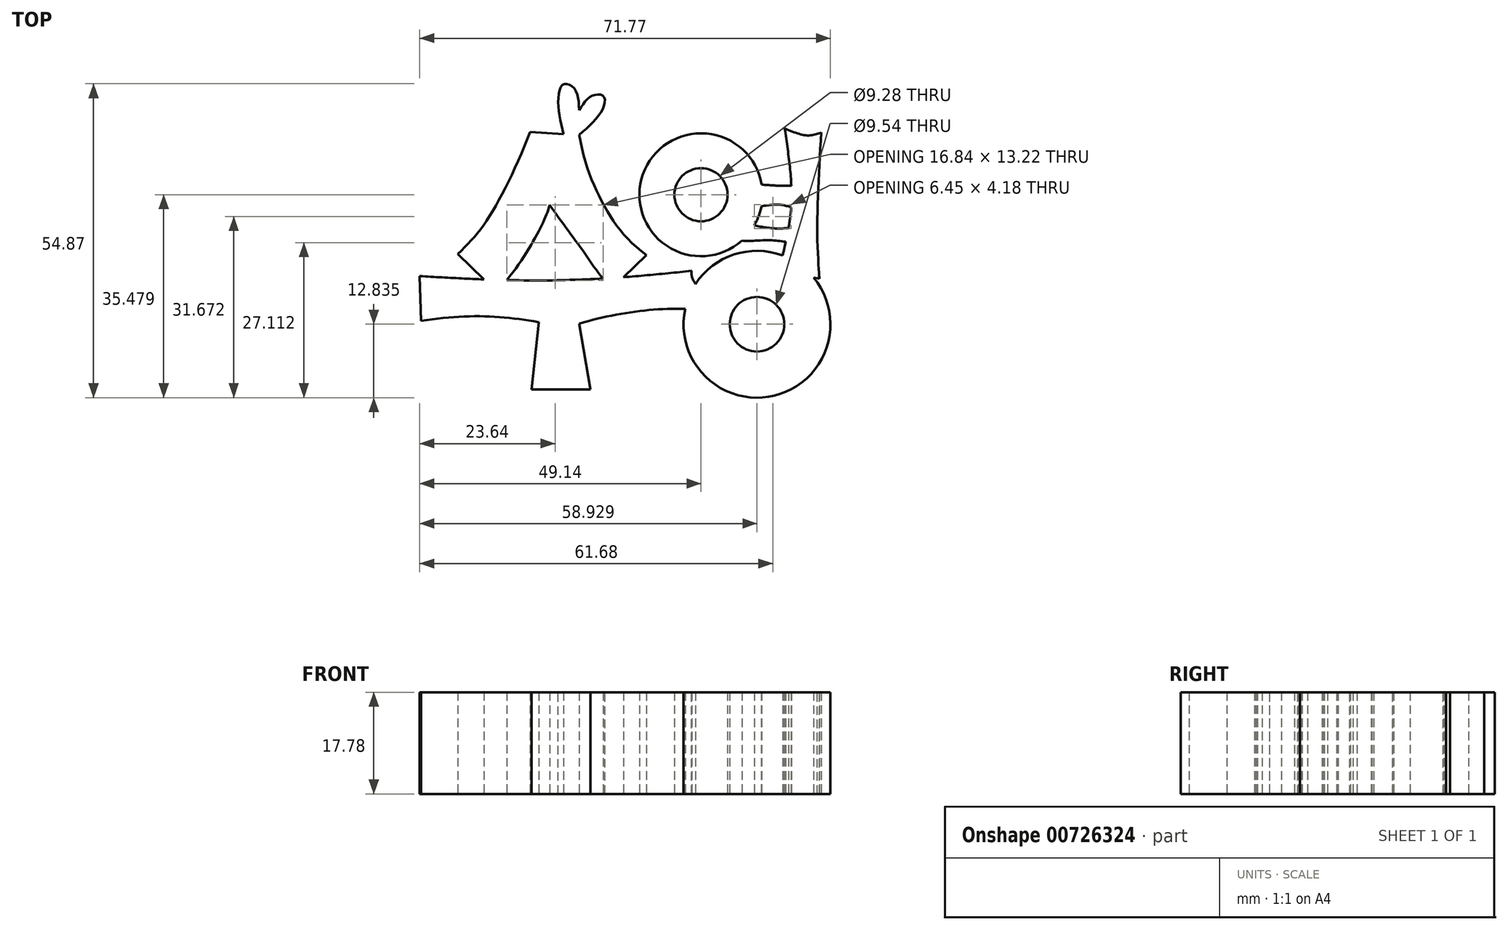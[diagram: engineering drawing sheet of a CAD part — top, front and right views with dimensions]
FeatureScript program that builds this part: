
annotation { "Feature Type Name" : "Feature", "Feature Type Description" : "" }
export const myFeature = defineFeature(function(context is Context, id is Id, definition is map)
    precondition{}
    {
        {
            var Q0;
            Q0=qCreatedBy(makeId("Top.planeOp"),FACE);
            var sketch = newSketch(context, id + "F0", { "sketchPlane" : qUnion([Q0])});
            skLineSegment(sketch, "E0", {"start": v(-29.82, 17.85) * mm, "end": v(-21.27, 17.36) * mm});
            skLineSegment(sketch, "E1", {"start": v(-42.52, -3.49) * mm, "end": v(-35.7, -10.02) * mm});
            skFitSpline(sketch, "E2", {"points": [v(-21.27, 17.36) * mm, v(-16.87, 4.89) * mm, v(-9.53, -3.67) * mm], "startDerivative": vector(4.76, -28.3) * mm, "endDerivative": vector(21.32, -15.57) * mm});
            skLineSegment(sketch, "E3", {"start": v(-9.53, -3.67) * mm, "end": v(-15.4, -9.29) * mm});
            skFitSpline(sketch, "E4", {"points": [v(-35.7, -10.02) * mm, v(-28.36, 0.49) * mm, v(-26.4, 5.13) * mm], "startDerivative": vector(15.3, 15.86) * mm, "endDerivative": vector(3.4, 11.19) * mm});
            skFitSpline(sketch, "E5", {"points": [v(-26.4, 5.13) * mm, v(-20.78, -2.69) * mm, v(-15.4, -9.29) * mm], "startDerivative": vector(10.2, -16.03) * mm, "endDerivative": vector(13.32, -9.78) * mm});
            skFitSpline(sketch, "E6", {"points": [v(-49.14, -7.33) * mm, v(-25.42, -8.07) * mm, v(-1.62, -6.4) * mm], "startDerivative": vector(47.36, -2.81) * mm, "endDerivative": vector(46.51, 5.27) * mm});
            skFitSpline(sketch, "E7", {"points": [v(-1.62, -6.4) * mm, v(0, -10.6) * mm, v(-1.1, -13.16) * mm], "startDerivative": vector(-1.95, -9.74) * mm, "endDerivative": vector(1.76, -4.5) * mm});
            skFitSpline(sketch, "E8", {"points": [v(-1.1, -13.16) * mm, v(-21.27, -15.65) * mm], "startDerivative": vector(-18.33, 1.47) * mm, "endDerivative": vector(-19.8, -5.87) * mm});
            skFitSpline(sketch, "E9", {"points": [v(-21.27, -15.65) * mm, v(-19.31, -27.13) * mm], "startDerivative": vector(1.96, -11.49) * mm, "endDerivative": vector(1.96, -11.49) * mm});
            skFitSpline(sketch, "E10", {"points": [v(-19.31, -27.13) * mm, v(-29.58, -27.13) * mm], "startDerivative": vector(-10.27, 0) * mm, "endDerivative": vector(-10.27, 0) * mm});
            skFitSpline(sketch, "E11", {"points": [v(-29.58, -27.13) * mm, v(-28.36, -15.4) * mm], "startDerivative": vector(1.22, 11.73) * mm, "endDerivative": vector(1.22, 11.73) * mm});
            skFitSpline(sketch, "E12", {"points": [v(-49.14, -7.33) * mm, v(-48.9, -15.16) * mm], "startDerivative": vector(0.24, -7.82) * mm, "endDerivative": vector(0.24, -7.82) * mm});
            skFitSpline(sketch, "E13", {"points": [v(-48.9, -15.16) * mm, v(-28.36, -15.4) * mm], "startDerivative": vector(22.73, 3.67) * mm, "endDerivative": vector(19.8, -3.67) * mm});
            skFitSpline(sketch, "E14", {"points": [v(-42.52, -3.49) * mm, v(-37.26, 2.62) * mm, v(-29.82, 17.85) * mm], "startDerivative": vector(15.27, 14.37) * mm, "endDerivative": vector(11.7, 29.4) * mm});
            skCircle(sketch, "E15", {"center": v(0, 6.89) * mm, "radius": 10.75 * mm});
            skCircle(sketch, "E16", {"center": v(0, 6.89) * mm, "radius": 4.64 * mm});
            skFitSpline(sketch, "E17", {"points": [v(8.92, 8.8) * mm, v(14.97, 8.44) * mm, v(17.91, 8.62) * mm], "startDerivative": vector(11.18, -0.88) * mm, "endDerivative": vector(6.52, 0.63) * mm});
            skFitSpline(sketch, "E18", {"points": [v(8.92, 4.47) * mm, v(13.6, 5.16) * mm, v(17.22, 4.12) * mm], "startDerivative": vector(9.15, 2.24) * mm, "endDerivative": vector(7.42, -3.02) * mm});
            skFitSpline(sketch, "E19", {"points": [v(8.4, 1.7) * mm, v(12.73, 1.01) * mm, v(16.7, 1.18) * mm], "startDerivative": vector(8.52, -1.79) * mm, "endDerivative": vector(8.07, 0.77) * mm});
            skFitSpline(sketch, "E20", {"points": [v(7.15, -1.14) * mm, v(12.04, -1.06) * mm, v(17.05, -1.75) * mm], "startDerivative": vector(9.68, -0.85) * mm, "endDerivative": vector(9.34, -1.92) * mm});
            skFitSpline(sketch, "E21", {"points": [v(14.63, 18.47) * mm, v(15.84, 6.54) * mm, v(14.97, -0.54) * mm, v(13.6, -6.6) * mm], "startDerivative": vector(4.6, -31.6) * mm, "endDerivative": vector(-4.98, -20.83) * mm});
            skFitSpline(sketch, "E22", {"points": [v(14.63, 18.47) * mm, v(18.6, 17.26) * mm, v(21.02, 17.78) * mm], "startDerivative": vector(7.46, -3.08) * mm, "endDerivative": vector(5.23, 1.92) * mm});
            skFitSpline(sketch, "E23", {"points": [v(21.02, 17.78) * mm, v(20.33, -0.72) * mm, v(20.68, -7.63) * mm, v(20.68, -7.8) * mm], "startDerivative": vector(-2.05, -33.37) * mm, "endDerivative": vector(-0.1, -2.02) * mm});
            skFitSpline(sketch, "E24", {"points": [v(20.68, -7.77) * mm, v(13.6, -6.6) * mm], "startDerivative": vector(-7.09, 1.17) * mm, "endDerivative": vector(-7.09, 1.17) * mm});
            skCircle(sketch, "E25", {"center": v(9.79, -15.75) * mm, "radius": 12.84 * mm});
            skCircle(sketch, "E26", {"center": v(9.79, -15.75) * mm, "radius": 4.77 * mm});
            skFitSpline(sketch, "E27", {"points": [v(-24.02, 17.51) * mm, v(-24.94, 23.39) * mm, v(-24, 26.2) * mm, v(-22.13, 25.45) * mm, v(-21.27, 21.7) * mm], "startDerivative": vector(-4.38, 18.73) * mm, "endDerivative": vector(0.94, -16.52) * mm});
            skFitSpline(sketch, "E28", {"points": [v(-21.27, 21.7) * mm, v(-19.12, 24.14) * mm, v(-17.06, 24.14) * mm, v(-17.25, 21.7) * mm, v(-21.27, 17.36) * mm], "startDerivative": vector(7.4, 11.87) * mm, "endDerivative": vector(-14.5, -12.63) * mm});
            skSolve(sketch);
        }
        {
            var Q0;
            {var subQ0=sQuery(id+"F0.wireOp",EDGE,"E9");Q0=makeQuery(id+"F0.imprint","IMPRINT",FACE,{"disambiguationData":[TD([[makeQuery(id+"F0.imprint","IMPRINT",EDGE,{"derivedFrom":subQ0}),-1.0]])]});}
            var Q1;
            {var subQ0=sQuery(id+"F0.wireOp",EDGE,"E5");var subQ1=sQuery(id+"F0.wireOp",EDGE,"E3");var subQ2=makeQuery(id+"F0.imprint","INTERSECT",VERTEX,{"derivedFrom":[subQ1,subQ0]});Q1=makeQuery(id+"F0.imprint","IMPRINT",FACE,{"disambiguationData":[TD([[makeQuery(id+"F0.imprint","IMPRINT",EDGE,{"disambiguationData":[TD([[subQ2,1.0]])],"derivedFrom":subQ1}),-1.0]])]});}
            var Q2;
            {var subQ0=sQuery(id+"F0.wireOp",EDGE,"E4");var subQ1=sQuery(id+"F0.wireOp",EDGE,"E1");var subQ2=makeQuery(id+"F0.imprint","INTERSECT",VERTEX,{"derivedFrom":[subQ1,subQ0]});Q2=makeQuery(id+"F0.imprint","IMPRINT",FACE,{"disambiguationData":[TD([[makeQuery(id+"F0.imprint","IMPRINT",EDGE,{"disambiguationData":[TD([[subQ2,1.0]])],"derivedFrom":subQ1}),1.0]])]});}
            var Q3;
            Q3=makeQuery(id+"F0.imprint","IMPRINT",FACE,{"disambiguationData":[TD([[makeQuery(id+"F0.imprint","IMPRINT",EDGE,{"derivedFrom":sQuery(id+"F0.wireOp",EDGE,"E0")}),-1.0]])]});
            var Q4;
            Q4=makeQuery(id+"F0.imprint","IMPRINT",FACE,{"disambiguationData":[TD([[makeQuery(id+"F0.imprint","IMPRINT",EDGE,{"derivedFrom":sQuery(id+"F0.wireOp",EDGE,"E16")}),-1.0]])]});
            var Q5;
            {var subQ0=sQuery(id+"F0.wireOp",EDGE,"E17");var subQ1=sQuery(id+"F0.wireOp",EDGE,"E15");var subQ2=makeQuery(id+"F0.imprint","INTERSECT",VERTEX,{"derivedFrom":[subQ1,subQ0]});Q5=makeQuery(id+"F0.imprint","IMPRINT",FACE,{"disambiguationData":[TD([[makeQuery(id+"F0.imprint","IMPRINT",EDGE,{"disambiguationData":[TD([[subQ2,1.0]])],"derivedFrom":subQ1}),-1.0]])]});}
            var Q6;
            {var subQ0=sQuery(id+"F0.wireOp",EDGE,"E8");var subQ1=sQuery(id+"F0.wireOp",EDGE,"E7");var subQ2=makeQuery(id+"F0.imprint","INTERSECT",VERTEX,{"derivedFrom":[subQ1,subQ0]});Q6=makeQuery(id+"F0.imprint","IMPRINT",FACE,{"disambiguationData":[TD([[makeQuery(id+"F0.imprint","IMPRINT",EDGE,{"disambiguationData":[TD([[subQ2,1.0]])],"derivedFrom":subQ1}),-1.0]])]});}
            var Q7;
            Q7=makeQuery(id+"F0.imprint","IMPRINT",FACE,{"disambiguationData":[TD([[makeQuery(id+"F0.imprint","IMPRINT",EDGE,{"derivedFrom":sQuery(id+"F0.wireOp",EDGE,"E26")}),-1.0]])]});
            var Q8;
            {var subQ0=sQuery(id+"F0.wireOp",EDGE,"E24");var subQ1=sQuery(id+"F0.wireOp",EDGE,"E21");var subQ2=makeQuery(id+"F0.imprint","INTERSECT",VERTEX,{"derivedFrom":[subQ1,subQ0]});Q8=makeQuery(id+"F0.imprint","IMPRINT",FACE,{"disambiguationData":[TD([[makeQuery(id+"F0.imprint","IMPRINT",EDGE,{"disambiguationData":[TD([[subQ2,1.0]])],"derivedFrom":subQ1}),1.0]])]});}
            var Q9;
            {var subQ6=sQuery(id+"F0.wireOp",EDGE,"E22");Q9=makeQuery(id+"F0.imprint","IMPRINT",FACE,{"disambiguationData":[TD([[makeQuery(id+"F0.imprint","IMPRINT",EDGE,{"derivedFrom":subQ6}),-1.0]])]});}
            var Q10;
            {var subQ0=sQuery(id+"F0.wireOp",EDGE,"E20");var subQ1=sQuery(id+"F0.wireOp",EDGE,"E15");var subQ2=makeQuery(id+"F0.imprint","INTERSECT",VERTEX,{"derivedFrom":[subQ1,subQ0]});Q10=makeQuery(id+"F0.imprint","IMPRINT",FACE,{"disambiguationData":[TD([[makeQuery(id+"F0.imprint","IMPRINT",EDGE,{"disambiguationData":[TD([[subQ2,-1.0]])],"derivedFrom":subQ1}),-1.0]])]});}
            var Q11;
            {var subQ2=sQuery(id+"F0.wireOp",EDGE,"E27");Q11=makeQuery(id+"F0.imprint","IMPRINT",FACE,{"disambiguationData":[TD([[makeQuery(id+"F0.imprint","IMPRINT",EDGE,{"derivedFrom":subQ2}),-1.0]])]});}
            extrude(context, id + "F1", {"entities" : qUnion([Q0, Q1, Q2, Q3, Q4, Q5, Q6, Q7, Q8, Q9, Q10, Q11]), "depth" : 17.78 * mm, "offsetDistance" : 25.4 * mm});
        }
    });
